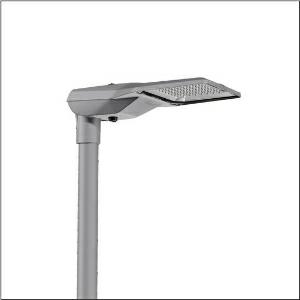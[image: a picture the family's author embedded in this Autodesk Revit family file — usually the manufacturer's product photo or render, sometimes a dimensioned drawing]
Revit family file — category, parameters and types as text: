
# Revit family: streetlight_sl_21_midi___stw1_0a_5xe3e43t08nb_27ab
name_source: partatom
category: Lighting Fixtures
units: mm (PartAtom-declared; Revit-internal decimal feet)

## family parameters
Cut with Voids When Loaded = No
Host = Face
Light Source = No
Part Type = Normal
Room Calculation Point = No
Round Connector Dimension = Use Diameter
Shared = No

## types (1)
- --- (1 x LED, 23710 lm, 151.2 W, 4000K)
    Apparent Load = 151 VA
    CIE Flux Codes = 39 75 98 100 100
    Color Rendering = 70
    Color Temperature = 4000K
    Default Elevation = 1800 mm
    Description = Streetlight SL 21 midi, mast luminaire, primary light control with lens, of PMMA, primary optical cover: cover, of toughened safety glass, transparent, light distribution: STW1.0a, light emission: direct distribution, primary light characteristic: asymmetric, installation type: side-entry, post-top, LED, High Power LED, rated luminous flux: 23.710lm, luminous efficacy: 157lm/W, light colour: 740, colour temperature: 4000K, control gear: D4i, control: overheat protection, constant luminous flux control, time-dependent luminous flux control, flexible luminous flux parameterisation, pre-setting: logarithmic dimming characteristic, mains connection: 230..240V, AC, 50/60Hz, start of lifetime: 151W, end of service life: 157W, reduction: 70W, luminaire housing, of diecast aluminium, powder-coated, Siteco® metallic grey (DB 702S), corrosivity category C5 mid according to DIN EN ISO 12944, please order mast flange separately, inclination adjustable: 0°, 5°, 10°, 15°, sealing non-destructively replaceable, multi-level sealing system, length: 644mm, width: 335mm, height: 110mm, mast flange for spigot size: 42mm (side-entry): 5XC10008XM4, 60/48mm (side-entry/post-top): 5XC10108XM2, 76/60mm (side-entry/post-top): 5XC10108XM1, mounting height: 4..8m, Smart Interface below and above, protection rating (complete): IP66, insulation class (complete): insulation class II (safety insulation), certification: CE, ENEC, ENEC+, VDE, impact resistance: IK10, permissible operating ambient temperature for outdoor applications: -40..+50°C, standard-compliant lighting for roads and squares, packaging unit: 1 piece

Light Distribution: STW1.0a
    Height = 111 mm
    Lamp = 1 x LED
    Lamp Light Flux = 23710 lm
    Lamp Power = 151.2 W
    Lamp count = 1
    Length = 644 mm
    Luminous efficacy = 157 lm/W
    Manufacturer = Siteco
    ModVariant = No
    Model = 5XE3E43T08NB
    Number of Poles = 1
    OnlyDefault = Yes
    Power Factor = 1
    Product Name = Streetlight SL 21 midi | STW1.0a
    Product group = mast luminaire | pylon top
    ProductGroupID = 6100
    Protection Class = Protection class II
    Protection Degree = IP 66
    RLX_Detail_Level = 1
    RLX_Emergency_Light_Flux = 0 lm
    RLX_Emergency_Type = 0
    RLX_Emergency_Type_DB = No
    RlxData = <blob elided: 27169 chars, md5=dad403cc>
    Socket = socket
    Standby Power = 0 W
    System Light Flux = 23710 lm
    System Power = 151 W
    Type Comments = factory setting: luminous flux: 100 % | dim-lin: 254 | 802 mA
    Type Image = l_1004304.jpg
    URL = http://relux.com
    VarID = @adj_169534
    Voltage = 0 V
    Weight = 0.00 kg
    Width = 336 mm

## geometry (parser evidence)
native form markers: Blend x4, Sweep x12
no freeform markers — native parametric forms only
